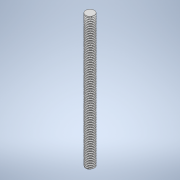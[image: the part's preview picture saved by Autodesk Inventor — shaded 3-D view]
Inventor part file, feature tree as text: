
AUTODESK INVENTOR PART (.ipt)
format: ipt  version: 2022 (Build 260153000, 153)  size: 1,042,432 bytes
history: native  units: mm
features: sketch x2, extrude x1, helix x1
ambient origin geometry x8: Origin, YZ Plane, XZ Plane, XY Plane, X Axis, Y Axis, Z Axis, Center Point
bodies: Solid1 (feature_tree)
feature tree (4):
  extrude  "Extrusion1"  Depth=152.4mm TaperAngle=0.0deg
  helix  "Coil1"  [1 undecoded]
  sketch  "Sketch1"  dims[d0=10.0mm d1=152.4mm d2=0.0mm d3=60.0deg]
  sketch  "Sketch2"  dims[d4=1.7mm d5=5.0mm d6=0.2mm d7=1.7mm d8=157.4mm d9=10.0mm d10=0.0mm d11=90.0deg d12=90.0deg d13=0.0mm d14=0.0mm]
note: 1 required parameter value undecoded (feature->parameter linkage not recoverable at this tier; creation-order binding heuristic only, values carry confidence <= 0.55)
